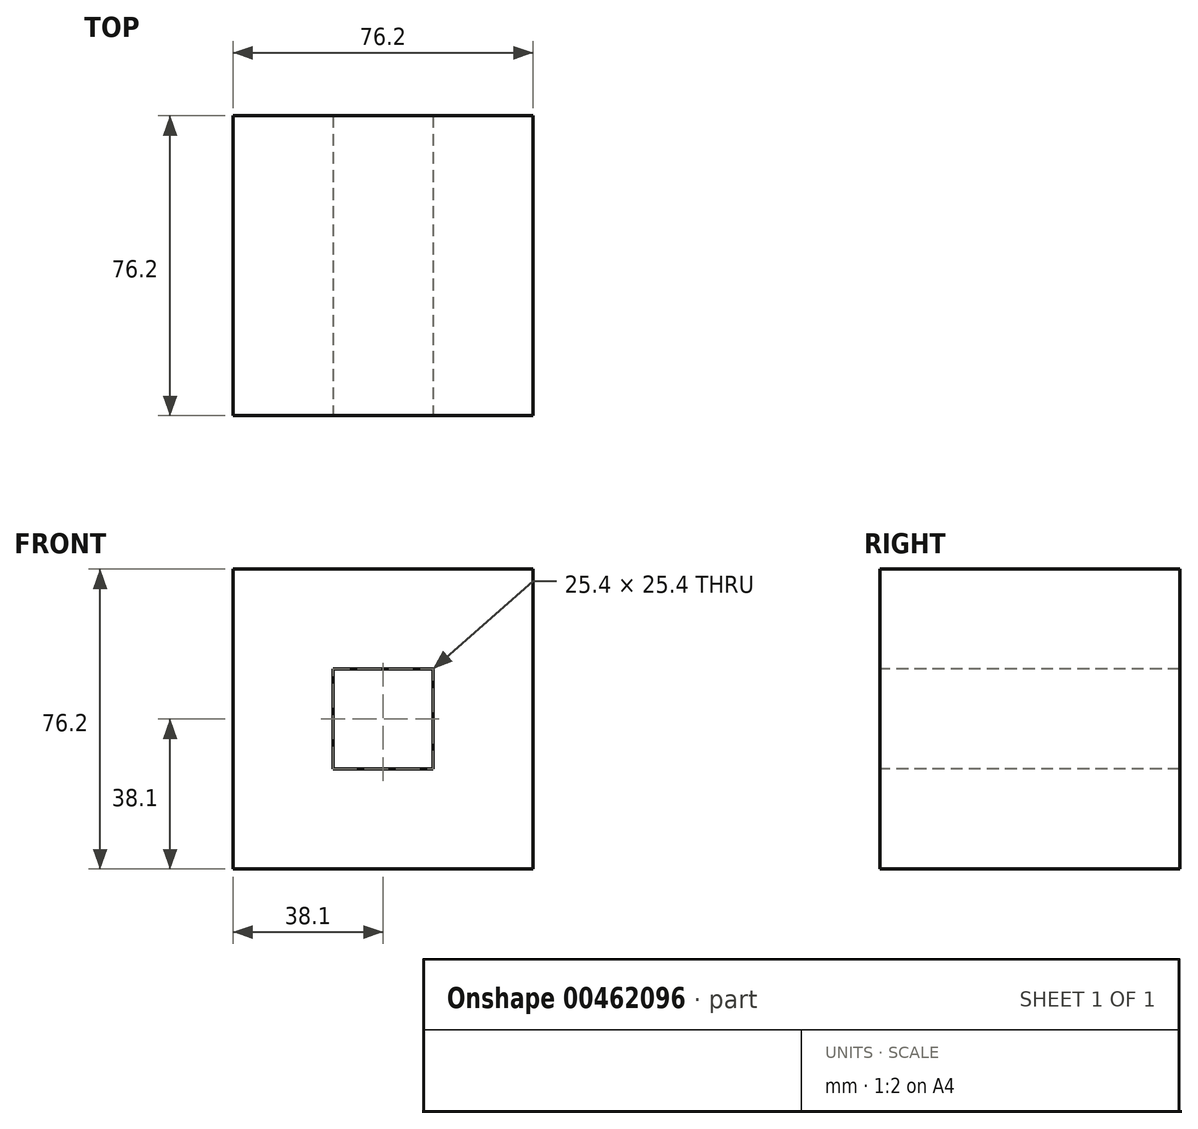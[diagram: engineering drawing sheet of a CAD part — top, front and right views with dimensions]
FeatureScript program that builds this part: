
annotation { "Feature Type Name" : "Feature", "Feature Type Description" : "" }
export const myFeature = defineFeature(function(context is Context, id is Id, definition is map)
    precondition{}
    {
        {
            var Q0;
            Q0=qCreatedBy(makeId("Front.planeOp"),FACE);
            var sketch = newSketch(context, id + "F0", { "sketchPlane" : qUnion([Q0])});
            skLineSegment(sketch, "E0.bottom", {"start": v(-38.1, 38.1) * mm, "end": v(38.1, 38.1) * mm});
            skLineSegment(sketch, "E0.top", {"start": v(-38.1, -38.1) * mm, "end": v(38.1, -38.1) * mm});
            skLineSegment(sketch, "E0.left", {"start": v(-38.1, 38.1) * mm, "end": v(-38.1, -38.1) * mm});
            skLineSegment(sketch, "E0.right", {"start": v(38.1, 38.1) * mm, "end": v(38.1, -38.1) * mm});
            skPoint(sketch, "E0.middle", {"position": v(0, 0) * mm});
            skSolve(sketch);
        }
        {
            var Q0;
            Q0=makeQuery(id+"F0.imprint","IMPRINT",FACE,{"disambiguationData":[TD([[makeQuery(id+"F0.imprint","IMPRINT",EDGE,{"derivedFrom":sQuery(id+"F0.wireOp",EDGE,"E0.bottom")}),-1.0]])]});
            extrude(context, id + "F1", {"entities" : qUnion([Q0]), "depth" : 76.2 * mm});
        }
        {
            var Q0;
            Q0=makeQuery(id+"F1.opExtrude","CAP_FACE",FACE,{"disambiguationData":[OSD([sQuery(id+"F0.wireOp",EDGE,"E0.bottom"),sQuery(id+"F0.wireOp",EDGE,"E0.top"),sQuery(id+"F0.wireOp",EDGE,"E0.left"),sQuery(id+"F0.wireOp",EDGE,"E0.right")])],"isStart":false});
            var sketch = newSketch(context, id + "F2", { "sketchPlane" : qUnion([Q0])});
            skLineSegment(sketch, "E1.bottom", {"start": v(-12.7, 12.7) * mm, "end": v(12.7, 12.7) * mm});
            skLineSegment(sketch, "E1.top", {"start": v(-12.7, -12.7) * mm, "end": v(12.7, -12.7) * mm});
            skLineSegment(sketch, "E1.left", {"start": v(-12.7, 12.7) * mm, "end": v(-12.7, -12.7) * mm});
            skLineSegment(sketch, "E1.right", {"start": v(12.7, 12.7) * mm, "end": v(12.7, -12.7) * mm});
            skPoint(sketch, "E1.middle", {"position": v(0, 0) * mm});
            skSolve(sketch);
        }
        {
            var Q0;
            Q0=makeQuery(id+"F2.imprint","IMPRINT",FACE,{"disambiguationData":[TD([[makeQuery(id+"F2.imprint","IMPRINT",EDGE,{"derivedFrom":sQuery(id+"F2.wireOp",EDGE,"E1.bottom")}),-1.0]])]});
            extrude(context, id + "F3", {"entities" : qUnion([Q0]), "operationType" : NewBodyOperationType.REMOVE, "oppositeDirection" : true, "depth" : 25.4 * mm});
        }
        {
            var Q0;
            Q0=makeQuery(id+"F3.boolean.opBoolean","COPY",FACE,{"derivedFrom":makeQuery(id+"F3.opExtrude","CAP_FACE",FACE,{"disambiguationData":[OSD([sQuery(id+"F2.wireOp",EDGE,"E1.bottom"),sQuery(id+"F2.wireOp",EDGE,"E1.top"),sQuery(id+"F2.wireOp",EDGE,"E1.left"),sQuery(id+"F2.wireOp",EDGE,"E1.right")])],"isStart":false})});
            extrude(context, id + "F4", {"entities" : qUnion([Q0]), "operationType" : NewBodyOperationType.REMOVE, "oppositeDirection" : true, "depth" : 25.4 * mm});
        }
        {
            var Q0;
            Q0=makeQuery(id+"F1.opExtrude","CAP_FACE",FACE,{"disambiguationData":[OSD([sQuery(id+"F0.wireOp",EDGE,"E0.bottom"),sQuery(id+"F0.wireOp",EDGE,"E0.top"),sQuery(id+"F0.wireOp",EDGE,"E0.left"),sQuery(id+"F0.wireOp",EDGE,"E0.right")])],"isStart":true});
            var sketch = newSketch(context, id + "F5", { "sketchPlane" : qUnion([Q0])});
            skLineSegment(sketch, "E2.bottom", {"start": v(-12.7, 12.7) * mm, "end": v(12.7, 12.7) * mm});
            skLineSegment(sketch, "E2.top", {"start": v(-12.7, -12.7) * mm, "end": v(12.7, -12.7) * mm});
            skLineSegment(sketch, "E2.left", {"start": v(-12.7, 12.7) * mm, "end": v(-12.7, -12.7) * mm});
            skLineSegment(sketch, "E2.right", {"start": v(12.7, 12.7) * mm, "end": v(12.7, -12.7) * mm});
            skPoint(sketch, "E2.middle", {"position": v(0, 0) * mm});
            skSolve(sketch);
        }
        {
            var Q0;
            Q0=makeQuery(id+"F5.imprint","IMPRINT",FACE,{"disambiguationData":[TD([[makeQuery(id+"F5.imprint","IMPRINT",EDGE,{"derivedFrom":sQuery(id+"F5.wireOp",EDGE,"E2.bottom")}),-1.0]])]});
            extrude(context, id + "F6", {"entities" : qUnion([Q0]), "operationType" : NewBodyOperationType.REMOVE, "oppositeDirection" : true, "depth" : 25.4 * mm});
        }
    });
